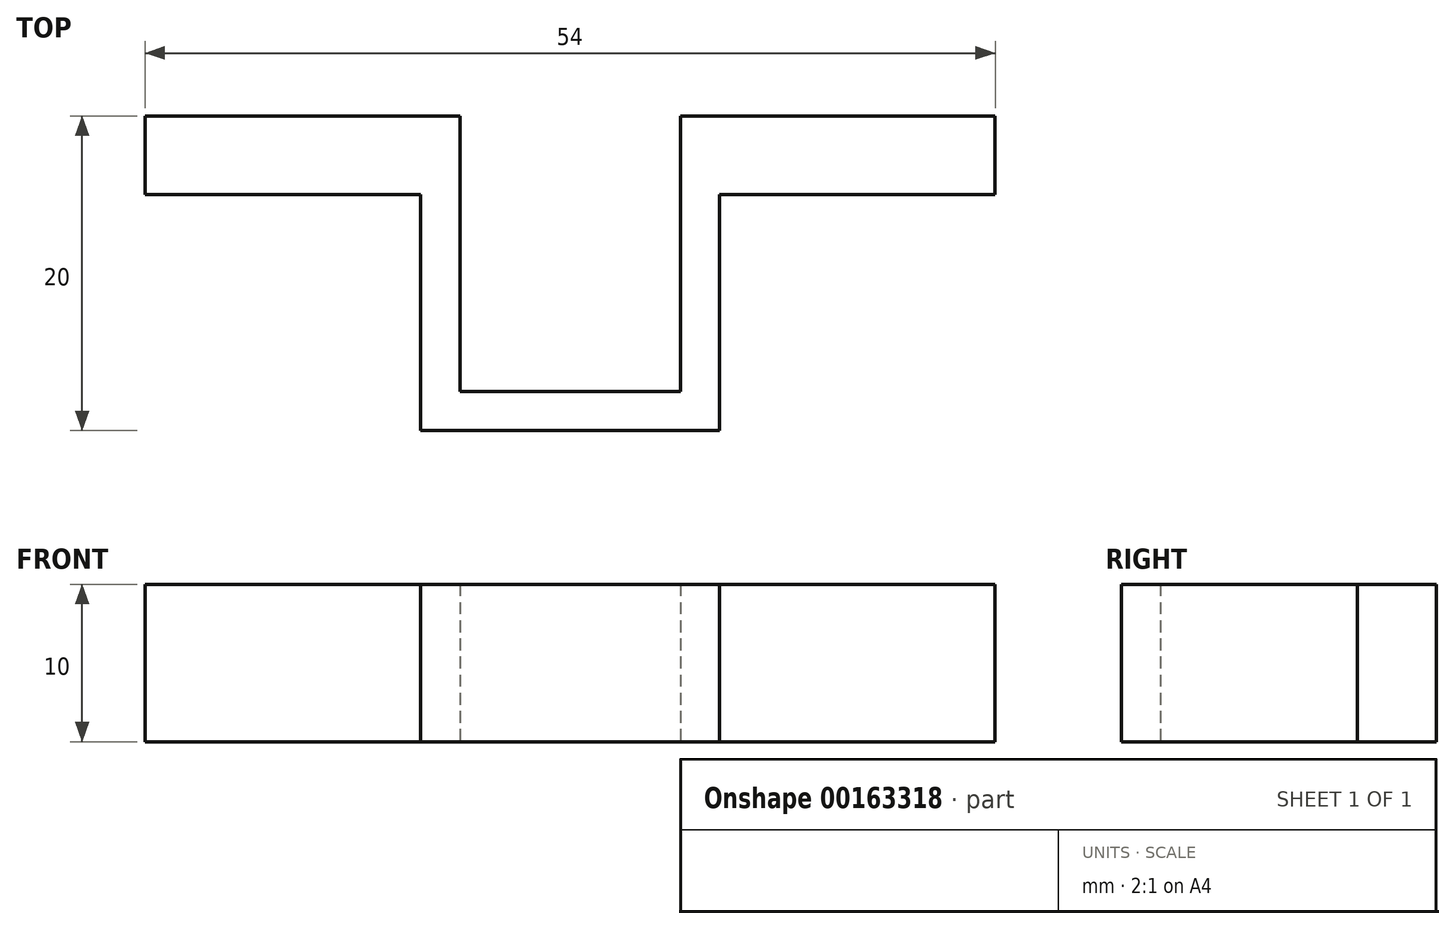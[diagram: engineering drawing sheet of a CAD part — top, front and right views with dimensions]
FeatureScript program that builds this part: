
annotation { "Feature Type Name" : "Feature", "Feature Type Description" : "" }
export const myFeature = defineFeature(function(context is Context, id is Id, definition is map)
    precondition{}
    {
        {
            var Q0;
            Q0=qCreatedBy(makeId("Top.planeOp"),FACE);
            var sketch = newSketch(context, id + "F0", { "sketchPlane" : qUnion([Q0])});
            skLineSegment(sketch, "E0.bottom", {"start": v(-4.05, 11.86) * mm, "end": v(15.95, 11.86) * mm});
            skLineSegment(sketch, "E0.top", {"start": v(-4.05, 6.86) * mm, "end": v(15.95, 6.86) * mm});
            skLineSegment(sketch, "E0.left", {"start": v(-4.05, 11.86) * mm, "end": v(-4.05, 6.86) * mm});
            skLineSegment(sketch, "E0.right", {"start": v(15.95, 11.86) * mm, "end": v(15.95, 6.86) * mm});
            skLineSegment(sketch, "E1.bottom", {"start": v(15.95, 11.86) * mm, "end": v(13.45, 11.86) * mm});
            skLineSegment(sketch, "E1.top", {"start": v(15.95, -8.14) * mm, "end": v(13.45, -8.14) * mm});
            skLineSegment(sketch, "E1.left", {"start": v(15.95, 11.86) * mm, "end": v(15.95, -8.14) * mm});
            skLineSegment(sketch, "E1.right", {"start": v(13.45, 11.86) * mm, "end": v(13.45, -8.14) * mm});
            skLineSegment(sketch, "E2.bottom", {"start": v(13.45, -8.14) * mm, "end": v(32.45, -8.14) * mm});
            skLineSegment(sketch, "E2.top", {"start": v(13.45, -5.64) * mm, "end": v(32.45, -5.64) * mm});
            skLineSegment(sketch, "E2.left", {"start": v(13.45, -8.14) * mm, "end": v(13.45, -5.64) * mm});
            skLineSegment(sketch, "E2.right", {"start": v(32.45, -8.14) * mm, "end": v(32.45, -5.64) * mm});
            skLineSegment(sketch, "E3.bottom", {"start": v(32.45, -8.14) * mm, "end": v(29.95, -8.14) * mm});
            skLineSegment(sketch, "E3.top", {"start": v(32.45, 11.86) * mm, "end": v(29.95, 11.86) * mm});
            skLineSegment(sketch, "E3.left", {"start": v(32.45, -8.14) * mm, "end": v(32.45, 11.86) * mm});
            skLineSegment(sketch, "E3.right", {"start": v(29.95, -8.14) * mm, "end": v(29.95, 11.86) * mm});
            skLineSegment(sketch, "E4.bottom", {"start": v(29.95, 11.86) * mm, "end": v(49.95, 11.86) * mm});
            skLineSegment(sketch, "E4.top", {"start": v(29.95, 6.86) * mm, "end": v(49.95, 6.86) * mm});
            skLineSegment(sketch, "E4.left", {"start": v(29.95, 11.86) * mm, "end": v(29.95, 6.86) * mm});
            skLineSegment(sketch, "E4.right", {"start": v(49.95, 11.86) * mm, "end": v(49.95, 6.86) * mm});
            skSolve(sketch);
        }
        {
            var Q0;
            Q0 = qSketchRegion(id + "F0", true);
            extrude(context, id + "F1", {"entities" : qUnion([Q0]), "depth" : 10 * mm});
        }
    });
